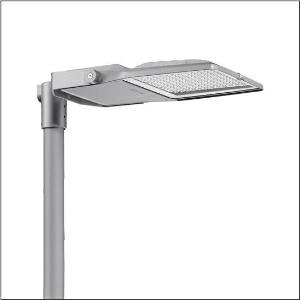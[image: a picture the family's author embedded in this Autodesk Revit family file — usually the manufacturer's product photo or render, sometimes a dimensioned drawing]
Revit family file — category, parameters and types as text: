
# Revit family: floodlight_fl_21_iq_midi___pl33t_5xa7781f4f3a_8e83
name_source: partatom
category: Lighting Fixtures
units: mm (PartAtom-declared; Revit-internal decimal feet)

## family parameters
Cut with Voids When Loaded = No
Host = Face
Light Source = No
Part Type = Normal
Room Calculation Point = No
Round Connector Dimension = Use Diameter
Shared = No

## types (1)
- --- (1 x LED, 36900 lm, 270.2 W, 4000K)
    Apparent Load = 270 VA
    CIE Flux Codes = 26 75 99 100 100
    Color Rendering = 70
    Color Temperature = 4000K
    Default Elevation = 1800 mm
    Description = Floodlight FL 21 iQ midi, floodlight, primary light control with lens, of PMMA, primary optical cover: protective disc, of toughened safety glass, transparent, light distribution: PL33T, light emission: direct distribution, installation type: surface-mounted, LED, High Power LED, rated luminous flux: 36.900lm, luminous efficacy: 137lm/W, light colour: 740, colour temperature: 4000K, control gear: ECG iQ, control: optimised constant luminous flux control (CLO 2.0), Desk-Remote (wireless, voltage-free reading and setting of iQ features in the workshop via application-optimized NFC function/RFID function), Light-Fading, Smart-Wire, Night-Set, Lumen-Switch, Temp-Guard, Auto-Match, with terminal, 6-pole, mains connection: 220..240V, AC, 50/60Hz, start of lifetime: 270W, end of service life: 287W, reduction: 118W, luminaire housing, of diecast aluminium, powder-coated, Siteco® metallic grey (DB 702S), corrosivity category C5 mid according to DIN EN ISO 12944, sealing non-destructively replaceable, please order mast flange separately, mast bracket, of steel, galvanised, powder-coated, Siteco® metallic grey (DB 702S), protection rating (complete): IP66, insulation class (complete): insulation class II (safety insulation), certification: CE, protection symbol: D, impact resistance: IK08, permissible operating ambient temperature: -40..+40°C, permissible operating ambient temperature for outdoor applications: -40..+50°C, standard: DIN EN 12944, LABS conformity tested according to VDMA 24364:2018-05, packaging unit: 1 piece

Light Distribution: PL33T
    Height = 76 mm
    Lamp = 1 x LED
    Lamp Light Flux = 36900 lm
    Lamp Power = 270.2 W
    Lamp count = 1
    Length = 657 mm
    Luminous efficacy = 137 lm/W
    Manufacturer = Siteco
    ModVariant = No
    Model = 5XA7781F4F3A
    Number of Poles = 1
    OnlyDefault = Yes
    Power Factor = 1
    Product Name = Floodlight FL 21 iQ midi | PL33T
    Product group = floodlight | pylon annexe
    ProductGroupID = 6200
    Protection Class = Protection class II
    Protection Degree = IP 66
    RLX_Detail_Level = 1
    RLX_Emergency_Light_Flux = 0 lm
    RLX_Emergency_Type = 0
    RLX_Emergency_Type_DB = No
    RlxData = <blob elided: 153609 chars, md5=e37939f5>
    Socket = socket
    Standby Power = 0 W
    System Light Flux = 36900 lm
    System Power = 270 W
    Type Comments = factory setting: luminous flux: 100 % | dim-lin: 254 | 620 mA
    Type Image = l_1007123.jpg
    URL = http://relux.com
    VarID = @adj_051773
    Voltage = 0 V
    Weight = 0.00 kg
    Width = 442 mm

## geometry (parser evidence)
native form markers: Blend x4, Sweep x14
no freeform markers — native parametric forms only
